# Revit family: Zaniboni-Diva-2_Inch_Aperture_40°-1
name_source: partatom
category: Lighting Fixtures
revit_build: Autodesk Revit 2016 (Build: 20150220_1215(x64)
units: mm (PartAtom-declared; Revit-internal decimal feet)

## family parameters
Cut with Voids When Loaded = No
Host = Face
Light Source = No
Part Type = Normal
Room Calculation Point = No
Round Connector Dimension = Use Diameter
Shared = No

## types (1)
- D1-D2TTN-0927A-2C-WS
    Assembly Code = E1020300
    Base Finish = ZBN - Metal Matte White
    Beam = 36°
    Body Finish = ZBN - Metal Matte White
    CRI = 80
    Default Elevation = 1"
    Description = 2 inch 3 Light Sources Adjustable 40°
    Diffuser Finish = ZBN - Metal Matte White
    Frame Finish = ZBN - Metal Matte White
    Kelvin = 3000°K
    Keynote = 12500
    Length = 9"
    Manufacturer = Zaniboni
    Mechanism Finish = ZBN - Plastic-Black
    Model = D1-D2TTN-0927A-2C-WS
    RD = Yes
    RQ = No
    RT = Yes
    SD = Yes
    SQ = No
    ST = Yes
    Screen Finish = ZBN - Glass
    Support Finish = ZBN - Metal Matte White
    Type Comments = Diva
    URL = www.zanibonilighting.com
    Voltage = 120 V
    Wattage Comments = 14W
    Width = 2 63/64"

## geometry (parser evidence)
native form markers: Sweep x5
no freeform markers — native parametric forms only
